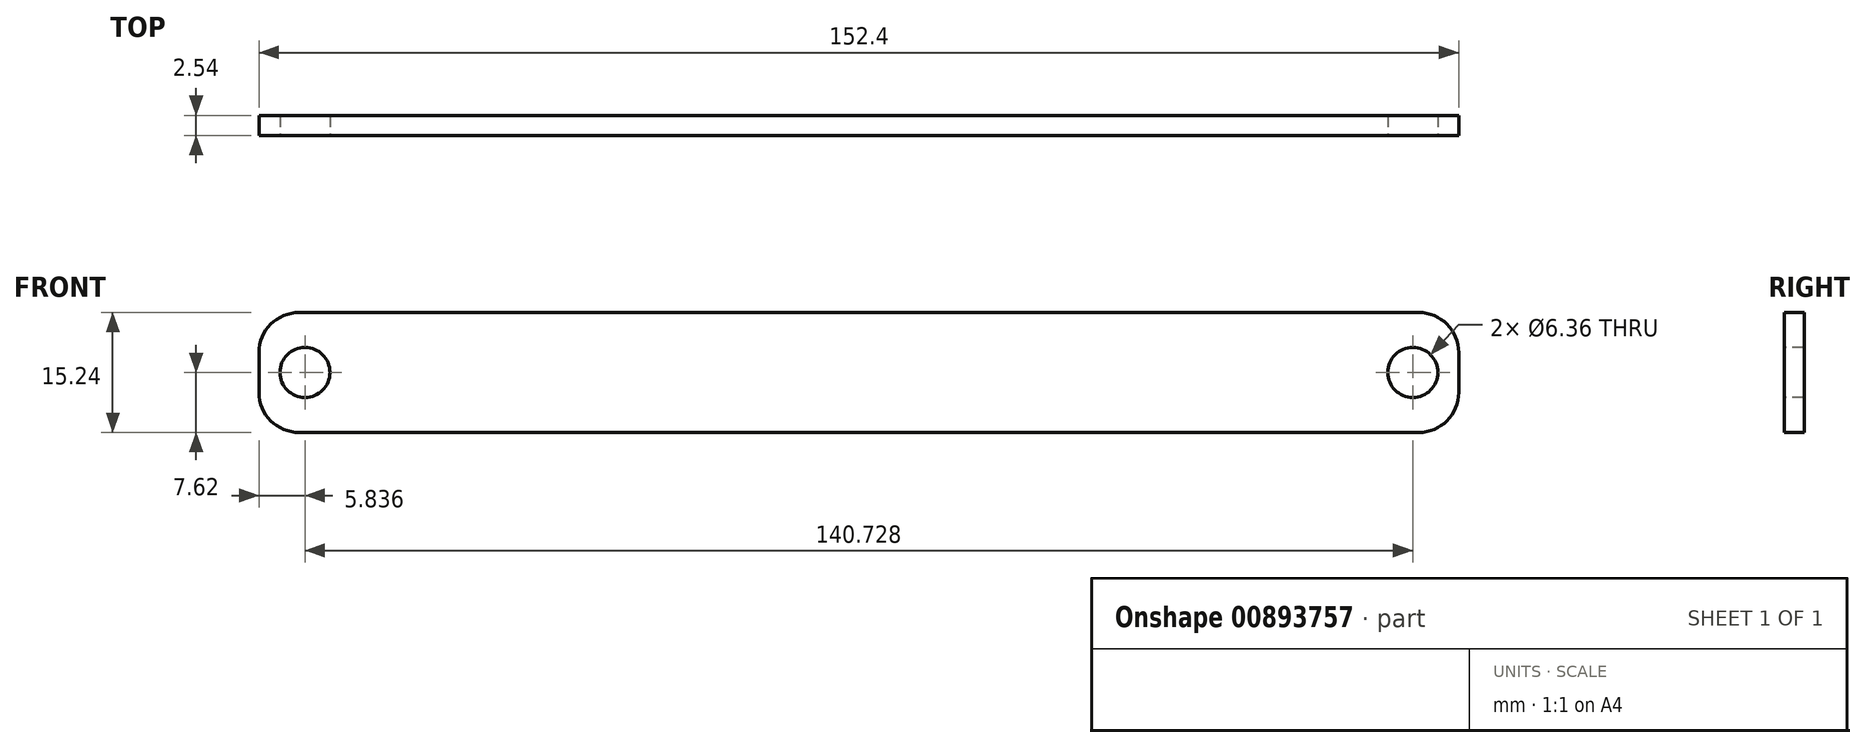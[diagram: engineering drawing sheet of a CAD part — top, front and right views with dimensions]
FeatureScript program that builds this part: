
annotation { "Feature Type Name" : "Feature", "Feature Type Description" : "" }
export const myFeature = defineFeature(function(context is Context, id is Id, definition is map)
    precondition{}
    {
        {
            var Q0;
            Q0=qCreatedBy(makeId("Front.planeOp"),FACE);
            var sketch = newSketch(context, id + "F0", { "sketchPlane" : qUnion([Q0])});
            skLineSegment(sketch, "E0.bottom", {"start": v(76.2, -7.62) * mm, "end": v(-76.2, -7.62) * mm});
            skLineSegment(sketch, "E0.top", {"start": v(76.2, 7.62) * mm, "end": v(-76.2, 7.62) * mm});
            skLineSegment(sketch, "E0.left", {"start": v(76.2, -7.62) * mm, "end": v(76.2, 7.62) * mm});
            skLineSegment(sketch, "E0.right", {"start": v(-76.2, -7.62) * mm, "end": v(-76.2, 7.62) * mm});
            skPoint(sketch, "E0.middle", {"position": v(0, 0) * mm});
            skSolve(sketch);
        }
        {
            var Q0;
            Q0 = qSketchRegion(id + "F0", true);
            extrude(context, id + "F1", {"entities" : qUnion([Q0]), "depth" : 2.54 * mm, "offsetDistance" : 25.4 * mm});
        }
        {
            var Q0;
            Q0=makeQuery(id+"F1.opExtrude","SWEPT_EDGE",EDGE,{"disambiguationData":[OSD([sQuery(id+"F0.wireOp",EDGE,"E0.top"),sQuery(id+"F0.wireOp",EDGE,"E0.right")])]});
            var Q1;
            Q1=makeQuery(id+"F1.opExtrude","SWEPT_EDGE",EDGE,{"disambiguationData":[OSD([sQuery(id+"F0.wireOp",EDGE,"E0.bottom"),sQuery(id+"F0.wireOp",EDGE,"E0.right")])]});
            var Q2;
            Q2=makeQuery(id+"F1.opExtrude","SWEPT_EDGE",EDGE,{"disambiguationData":[OSD([sQuery(id+"F0.wireOp",EDGE,"E0.top"),sQuery(id+"F0.wireOp",EDGE,"E0.left")])]});
            var Q3;
            Q3=makeQuery(id+"F1.opExtrude","SWEPT_EDGE",EDGE,{"disambiguationData":[OSD([sQuery(id+"F0.wireOp",EDGE,"E0.bottom"),sQuery(id+"F0.wireOp",EDGE,"E0.left")])]});
            fillet(context, id + "F2", {"entities" : qUnion([Q0, Q1, Q2, Q3]), "radius" : 5.08 * mm, "tangentPropagation" : true, "allowEdgeOverflow" : false});
        }
        {
            var Q0;
            Q0=makeQuery(id+"F1.opExtrude","CAP_FACE",FACE,{"disambiguationData":[OSD([sQuery(id+"F0.wireOp",EDGE,"E0.bottom"),sQuery(id+"F0.wireOp",EDGE,"E0.top"),sQuery(id+"F0.wireOp",EDGE,"E0.left"),sQuery(id+"F0.wireOp",EDGE,"E0.right")])],"isStart":false});
            var sketch = newSketch(context, id + "F3", { "sketchPlane" : qUnion([Q0])});
            skCircle(sketch, "E1", {"center": v(-70.36, 0) * mm, "radius": 3.18 * mm});
            skCircle(sketch, "E2.MirrorC", {"center": v(70.36, 0) * mm, "radius": 3.18 * mm});
            skSolve(sketch);
        }
        {
            var Q0;
            Q0 = qSketchRegion(id + "F3", true);
            extrude(context, id + "F4", {"entities" : qUnion([Q0]), "operationType" : NewBodyOperationType.REMOVE, "oppositeDirection" : true, "depth" : 25.4 * mm, "offsetDistance" : 25.4 * mm});
        }
    });
